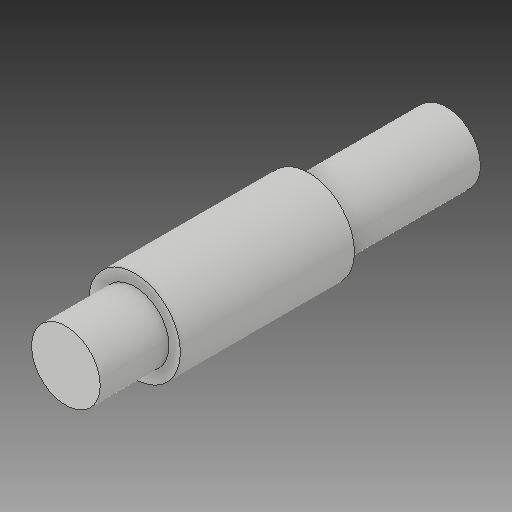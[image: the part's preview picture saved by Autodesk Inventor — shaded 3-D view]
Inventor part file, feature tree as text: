
AUTODESK INVENTOR PART (.ipt)
format: ipt  version: 2019 (Build 230136000, 136)  size: 110,080 bytes
history: native  units: mm
features: extrude x3, sketch x3
ambient origin geometry x8: Origin, YZ Plane, XZ Plane, XY Plane, X Axis, Y Axis, Z Axis, Center Point
bodies: Solid1 (feature_tree)
feature tree (6):
  extrude  "Extrusion1"  Depth=38.0mm TaperAngle=0.0deg
  extrude  "Extrusion2"  Depth=15.0mm TaperAngle=0.0deg
  extrude  "Extrusion3"  Depth=30.0mm TaperAngle=0.0deg
  sketch  "Sketch1"  dims[d0=20.0mm d1=38.0mm d2=0.0mm]
  sketch  "Sketch2"  dims[d3=15.0mm d4=15.0mm d5=0.0mm]
  sketch  "Sketch3"  dims[d7=15.0mm d8=30.0mm d9=0.0mm]
